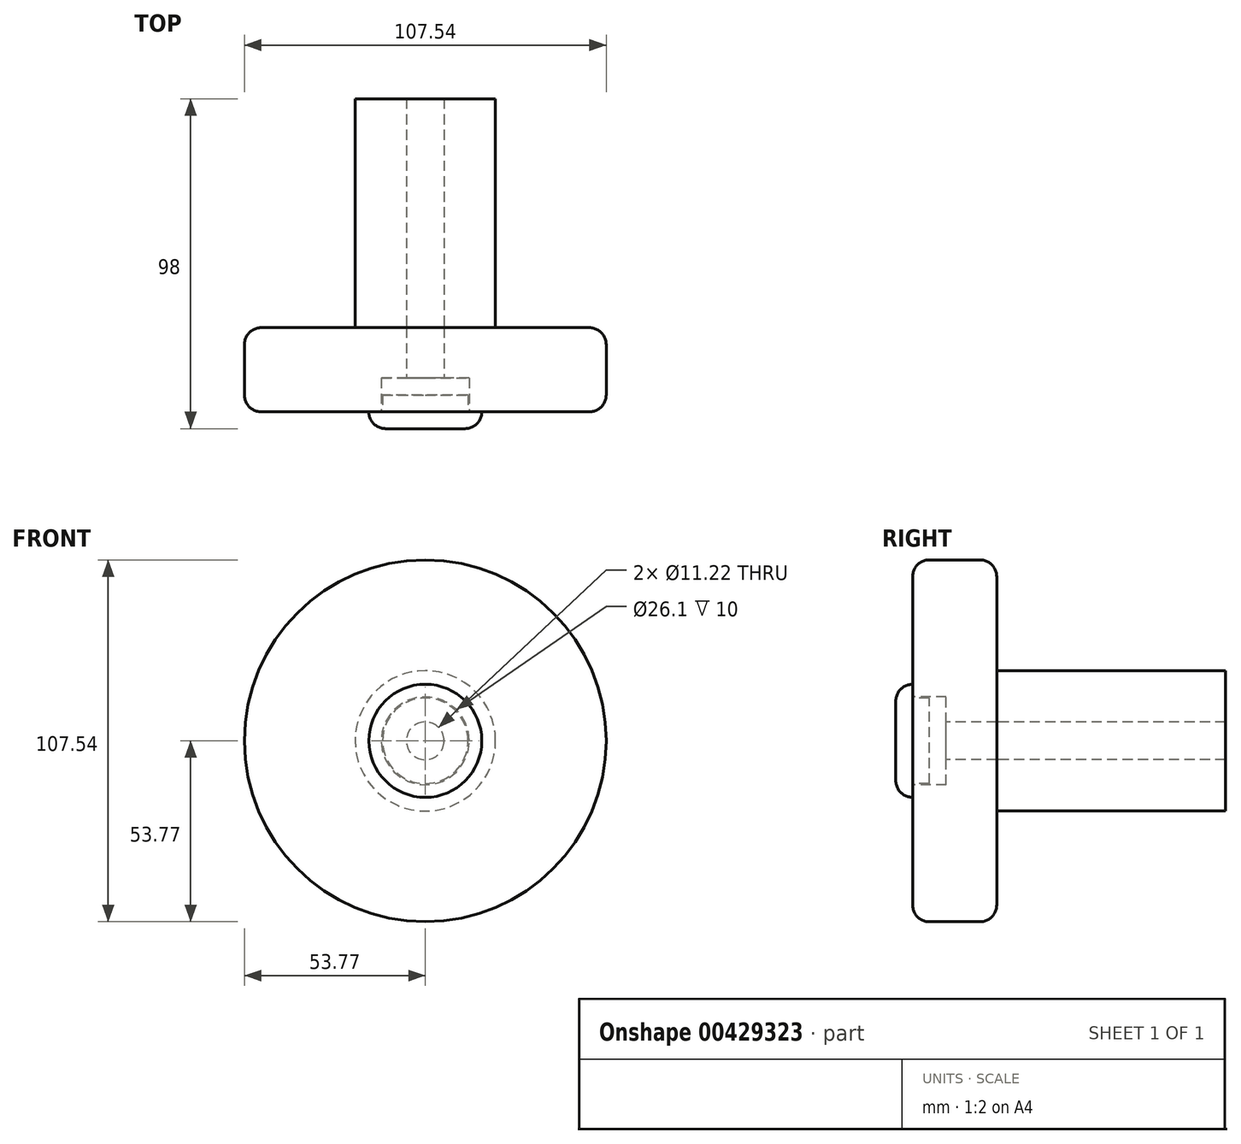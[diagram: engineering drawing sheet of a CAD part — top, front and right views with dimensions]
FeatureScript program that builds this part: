
annotation { "Feature Type Name" : "Feature", "Feature Type Description" : "" }
export const myFeature = defineFeature(function(context is Context, id is Id, definition is map)
    precondition{}
    {
        {
            var Q0;
            Q0=qCreatedBy(makeId("Front.planeOp"),FACE);
            var sketch = newSketch(context, id + "F0", { "sketchPlane" : qUnion([Q0])});
            skCircle(sketch, "E0", {"center": v(0, 0) * mm, "radius": 20.86 * mm});
            skSolve(sketch);
        }
        {
            var Q0;
            Q0=makeQuery(id+"F0.imprint","IMPRINT",FACE,{"disambiguationData":[TD([[makeQuery(id+"F0.imprint","IMPRINT",EDGE,{"derivedFrom":sQuery(id+"F0.wireOp",EDGE,"E0")}),1.0]])]});
            extrude(context, id + "F1", {"entities" : qUnion([Q0]), "depth" : 68 * mm});
        }
        {
            var Q0;
            Q0=makeQuery(id+"F1.opExtrude","CAP_FACE",FACE,{"disambiguationData":[OSD([sQuery(id+"F0.wireOp",EDGE,"E0")])],"isStart":false});
            var sketch = newSketch(context, id + "F2", { "sketchPlane" : qUnion([Q0])});
            skCircle(sketch, "E1", {"center": v(0, 0) * mm, "radius": 53.77 * mm});
            skSolve(sketch);
        }
        {
            var Q0;
            Q0=makeQuery(id+"F2.imprint","IMPRINT",FACE,{"disambiguationData":[TD([[makeQuery(id+"F2.imprint","IMPRINT",EDGE,{"derivedFrom":sQuery(id+"F2.wireOp",EDGE,"E1")}),1.0]])]});
            var Q1;
            Q1=makeQuery(id+"F2.imprint","IMPRINT",FACE,{"disambiguationData":[TD([[makeQuery(id+"F2.imprint","IMPRINT",EDGE,{"derivedFrom":makeQuery(id+"F1.opExtrude","CAP_EDGE",EDGE,{"disambiguationData":[OSD([sQuery(id+"F0.wireOp",EDGE,"E0")])],"isStart":false})}),1.0]])]});
            extrude(context, id + "F3", {"entities" : qUnion([Q0, Q1]), "depth" : 25 * mm});
        }
        {
            var Q0;
            Q0=makeQuery(id+"F3.opExtrude","CAP_FACE",FACE,{"disambiguationData":[OSD([sQuery(id+"F2.wireOp",EDGE,"E1")])],"isStart":false});
            var sketch = newSketch(context, id + "F4", { "sketchPlane" : qUnion([Q0])});
            skCircle(sketch, "E2", {"center": v(0, 0) * mm, "radius": 5.61 * mm});
            skSolve(sketch);
        }
        {
            var Q0;
            Q0 = qSketchRegion(id + "F4", true);
            extrude(context, id + "F5", {"entities" : qUnion([Q0]), "endBound" : BoundingType.THROUGH_ALL, "oppositeDirection" : true, "depth" : 74 * mm});
        }
        {
            var Q0;
            Q0=makeQuery(id+"F5.opExtrude","SWEPT_BODY",BODY,{"disambiguationData":[OSD([sQuery(id+"F4.wireOp",EDGE,"E2")])]});
            var Q1;
            Q1=makeQuery(id+"F1.opExtrude","SWEPT_BODY",BODY,{"disambiguationData":[OSD([sQuery(id+"F0.wireOp",EDGE,"E0")])]});
            var Q2;
            Q2=makeQuery(id+"F3.opExtrude","SWEPT_BODY",BODY,{"disambiguationData":[OSD([sQuery(id+"F2.wireOp",EDGE,"E1")])]});
            booleanBodies(context, id + "F6", {"operationType" : BooleanOperationType.SUBTRACTION, "tools" : qUnion([Q0]), "targets" : qUnion([Q1, Q2])});
        }
        {
            var Q0;
            Q0=makeQuery(id+"F3.opExtrude","CAP_EDGE",EDGE,{"disambiguationData":[OSD([sQuery(id+"F2.wireOp",EDGE,"E1")])],"isStart":false});
            var Q1;
            Q1=makeQuery(id+"F3.opExtrude","CAP_EDGE",EDGE,{"disambiguationData":[OSD([sQuery(id+"F2.wireOp",EDGE,"E1")])],"isStart":true});
            fillet(context, id + "F7", {"entities" : qUnion([Q0, Q1]), "radius" : 5 * mm, "tangentPropagation" : true, "allowEdgeOverflow" : false});
        }
        {
            var Q0;
            Q0=makeQuery(id+"F3.opExtrude","CAP_FACE",FACE,{"disambiguationData":[OSD([sQuery(id+"F2.wireOp",EDGE,"E1")])],"isStart":false});
            var sketch = newSketch(context, id + "F8", { "sketchPlane" : qUnion([Q0])});
            skCircle(sketch, "E3", {"center": v(0, 0) * mm, "radius": 13.05 * mm});
            skSolve(sketch);
        }
        {
            var Q0;
            Q0=makeQuery(id+"F8.imprint","IMPRINT",FACE,{"disambiguationData":[TD([[makeQuery(id+"F8.imprint","IMPRINT",EDGE,{"derivedFrom":sQuery(id+"F8.wireOp",EDGE,"E3")}),1.0]])]});
            extrude(context, id + "F9", {"entities" : qUnion([Q0]), "operationType" : NewBodyOperationType.REMOVE, "oppositeDirection" : true, "depth" : 10 * mm});
        }
        {
            var Q0;
            Q0=makeQuery(id+"F3.opExtrude","CAP_FACE",FACE,{"disambiguationData":[OSD([sQuery(id+"F2.wireOp",EDGE,"E1")])],"isStart":false});
            var sketch = newSketch(context, id + "F10", { "sketchPlane" : qUnion([Q0])});
            skCircle(sketch, "E4", {"center": v(0, 0) * mm, "radius": 12.7 * mm});
            skCircle(sketch, "E5", {"center": v(0, 0) * mm, "radius": 16.8 * mm});
            skSolve(sketch);
        }
        {
            var Q0;
            Q0=makeQuery(id+"F10.imprint","IMPRINT",FACE,{"disambiguationData":[TD([[makeQuery(id+"F10.imprint","IMPRINT",EDGE,{"derivedFrom":sQuery(id+"F10.wireOp",EDGE,"E4")}),1.0]])]});
            extrude(context, id + "F11", {"entities" : qUnion([Q0]), "oppositeDirection" : true, "depth" : 5 * mm});
        }
        {
            var Q0;
            Q0=makeQuery(id+"F10.imprint","IMPRINT",FACE,{"disambiguationData":[TD([[makeQuery(id+"F10.imprint","IMPRINT",EDGE,{"derivedFrom":sQuery(id+"F10.wireOp",EDGE,"E4")}),1.0]])]});
            var Q1;
            Q1=makeQuery(id+"F10.imprint","IMPRINT",FACE,{"disambiguationData":[TD([[makeQuery(id+"F10.imprint","IMPRINT",EDGE,{"derivedFrom":sQuery(id+"F10.wireOp",EDGE,"E5")}),1.0]])]});
            var Q2;
            Q2=makeQuery(id+"F10.imprint","IMPRINT",FACE,{"disambiguationData":[TD([[makeQuery(id+"F10.imprint","IMPRINT",EDGE,{"derivedFrom":sQuery(id+"F10.wireOp",EDGE,"E4")}),-1.0]])]});
            extrude(context, id + "F12", {"entities" : qUnion([Q0, Q1, Q2]), "operationType" : NewBodyOperationType.ADD, "depth" : 5 * mm});
        }
        {
            var Q0;
            Q0=makeQuery(id+"F12.opExtrude","CAP_EDGE",EDGE,{"disambiguationData":[OSD([sQuery(id+"F10.wireOp",EDGE,"E5")])],"isStart":false});
            fillet(context, id + "F13", {"entities" : qUnion([Q0]), "radius" : 5 * mm, "tangentPropagation" : true, "allowEdgeOverflow" : false});
        }
    });
